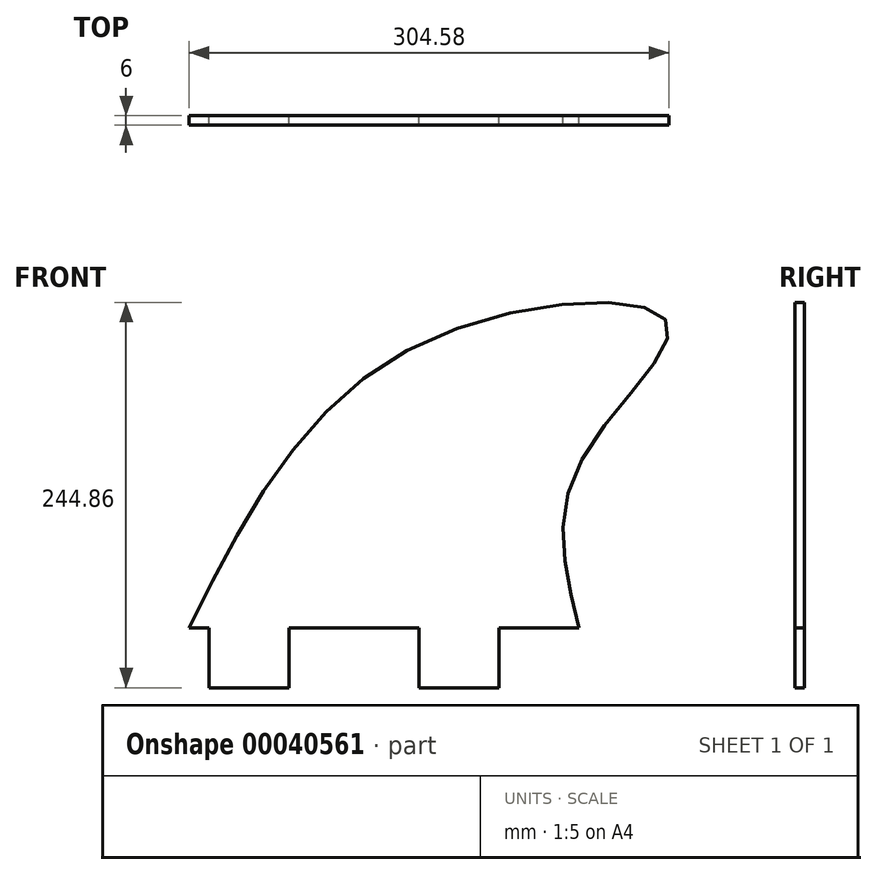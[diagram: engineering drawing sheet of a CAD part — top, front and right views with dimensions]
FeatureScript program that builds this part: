
annotation { "Feature Type Name" : "Feature", "Feature Type Description" : "" }
export const myFeature = defineFeature(function(context is Context, id is Id, definition is map)
    precondition{}
    {
        {
            var Q0;
            Q0=qCreatedBy(makeId("Front.planeOp"),FACE);
            var sketch = newSketch(context, id + "F0", { "sketchPlane" : qUnion([Q0])});
            skLineSegment(sketch, "E0", {"start": v(-146.05, -103.67) * mm, "end": v(-133.35, -103.67) * mm});
            skLineSegment(sketch, "E1", {"start": v(-133.35, -103.67) * mm, "end": v(-133.35, -141.77) * mm});
            skLineSegment(sketch, "E2", {"start": v(-133.35, -141.77) * mm, "end": v(-82.55, -141.77) * mm});
            skLineSegment(sketch, "E3", {"start": v(-82.55, -141.77) * mm, "end": v(-82.55, -103.67) * mm});
            skLineSegment(sketch, "E4", {"start": v(-82.55, -103.67) * mm, "end": v(0, -103.67) * mm});
            skLineSegment(sketch, "E5", {"start": v(0, -103.67) * mm, "end": v(0, -141.77) * mm});
            skLineSegment(sketch, "E6", {"start": v(0, -141.77) * mm, "end": v(50.8, -141.77) * mm});
            skLineSegment(sketch, "E7", {"start": v(50.8, -141.77) * mm, "end": v(50.8, -103.67) * mm});
            skLineSegment(sketch, "E8", {"start": v(50.8, -103.67) * mm, "end": v(101.6, -103.67) * mm});
            skLineSegment(sketch, "E9", {"start": v(101.6, -103.67) * mm, "end": v(237.1, -103.67) * mm, "construction": true});
            skFitSpline(sketch, "E10", {"points": [v(101.6, -103.67) * mm, v(101.6, 0) * mm, v(157.75, 89.63) * mm, v(0, 76.46) * mm, v(-146.05, -103.67) * mm], "startDerivative": vector(-126.97, 487.84) * mm, "endDerivative": vector(-341.36, -684.87) * mm});
            skSolve(sketch);
        }
        {
            var Q0;
            Q0=makeQuery(id+"F0.imprint","IMPRINT",FACE,{"disambiguationData":[TD([[makeQuery(id+"F0.imprint","IMPRINT",EDGE,{"derivedFrom":sQuery(id+"F0.wireOp",EDGE,"E0")}),1.0]])]});
            extrude(context, id + "F1", {"entities" : qUnion([Q0]), "depth" : 6 * mm});
        }
        {
            var Q0;
            Q0=makeQuery(id+"F0.imprint","IMPRINT",FACE,{"disambiguationData":[TD([[makeQuery(id+"F0.imprint","IMPRINT",EDGE,{"derivedFrom":sQuery(id+"F0.wireOp",EDGE,"E0")}),1.0]])]});
            extrude(context, id + "F2", {"entities" : qUnion([Q0]), "operationType" : NewBodyOperationType.ADD, "depth" : 3.05 * mm});
        }
    });
